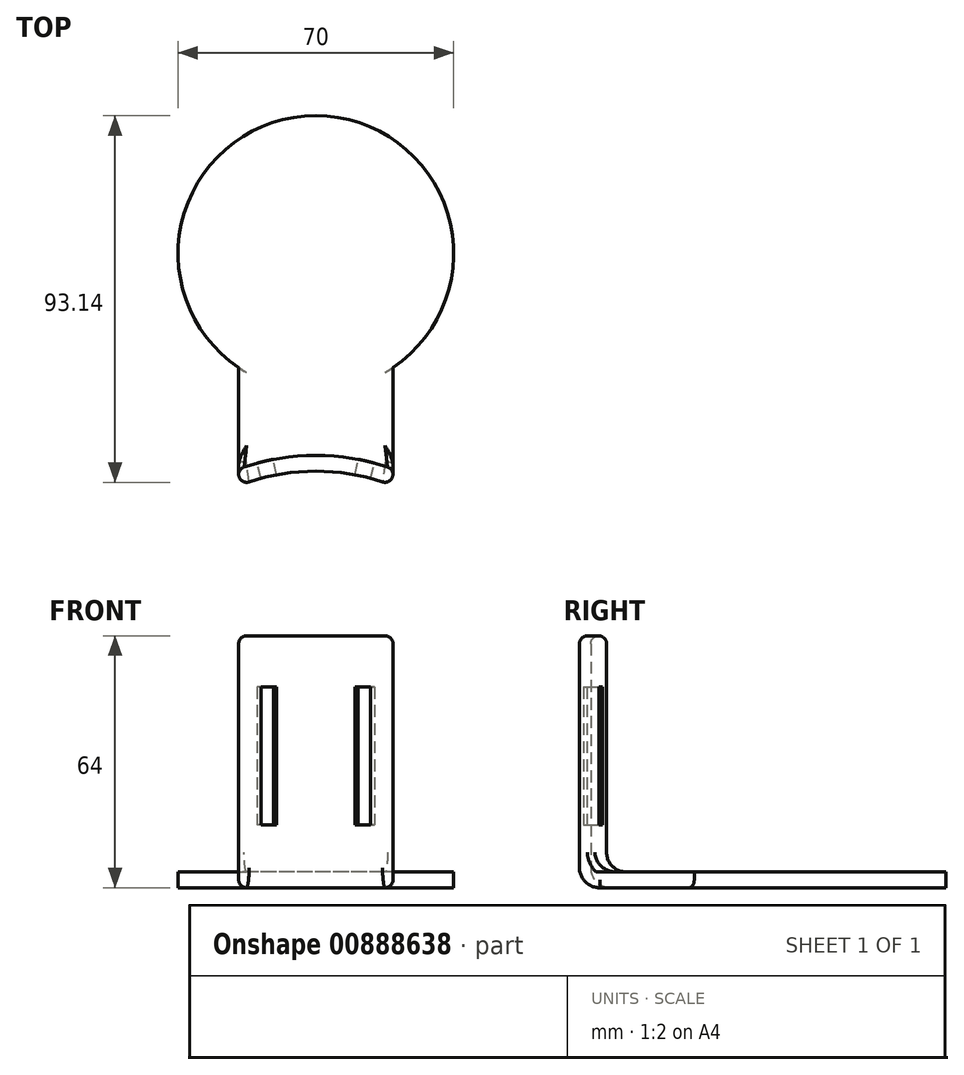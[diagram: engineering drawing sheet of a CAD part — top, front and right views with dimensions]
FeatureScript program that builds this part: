
annotation { "Feature Type Name" : "Feature", "Feature Type Description" : "" }
export const myFeature = defineFeature(function(context is Context, id is Id, definition is map)
    precondition{}
    {
        {
            var Q0;
            Q0=qCreatedBy(makeId("Top.planeOp"),FACE);
            var sketch = newSketch(context, id + "F0", { "sketchPlane" : qUnion([Q0])});
            skCircle(sketch, "E0", {"center": v(0, 0) * mm, "radius": 35 * mm});
            skLineSegment(sketch, "E1", {"start": v(0, 0) * mm, "end": v(0, -81.88) * mm, "construction": true});
            skLineSegment(sketch, "E2", {"start": v(19.6, -29) * mm, "end": v(19.6, -59) * mm});
            skLineSegment(sketch, "E3.MirrorCS", {"start": v(-19.6, -29) * mm, "end": v(-19.6, -59) * mm});
            skLineSegment(sketch, "E4", {"start": v(-35.4, 35) * mm, "end": v(46.06, 35) * mm, "construction": true});
            skArc(sketch, "E5", {"start": v(19.6, -59) * mm, "mid": v(0, -55.28) * mm, "end": v(-19.6, -59) * mm});
            skPoint(sketch, "E6", {"position": v(10, -56.22) * mm});
            skPoint(sketch, "E7", {"position": v(13.9, -57.12) * mm});
            skPoint(sketch, "E8.MirrorP", {"position": v(-10, -56.22) * mm});
            skPoint(sketch, "E9.MirrorP", {"position": v(-13.9, -57.12) * mm});
            skArc(sketch, "E10.0", {"start": v(19.6, -54.72) * mm, "mid": v(0, -51.28) * mm, "end": v(-19.6, -54.72) * mm});
            skSolve(sketch);
        }
        {
            var Q0;
            {var subQ0=sQuery(id+"F0.wireOp",EDGE,"E0");var subQ1=makeQuery(id+"F0.imprint","INTERSECT",VERTEX,{"derivedFrom":[subQ0,sQuery(id+"F0.wireOp",EDGE,"E2")]});Q0=makeQuery(id+"F0.imprint","IMPRINT",FACE,{"disambiguationData":[TD([[makeQuery(id+"F0.imprint","IMPRINT",EDGE,{"disambiguationData":[TD([[subQ1,1.0]])],"derivedFrom":subQ0}),1.0]])]});}
            var Q1;
            {var subQ5=sQuery(id+"F0.wireOp",EDGE,"E10.0");Q1=makeQuery(id+"F0.imprint","IMPRINT",FACE,{"disambiguationData":[TD([[makeQuery(id+"F0.imprint","IMPRINT",EDGE,{"derivedFrom":subQ5}),-1.0]])]});}
            var Q2;
            {var subQ0=sQuery(id+"F0.wireOp",EDGE,"E5");Q2=makeQuery(id+"F0.imprint","IMPRINT",FACE,{"disambiguationData":[TD([[makeQuery(id+"F0.imprint","IMPRINT",EDGE,{"derivedFrom":subQ0}),-1.0]])]});}
            extrude(context, id + "F1", {"entities" : qUnion([Q0, Q1, Q2]), "depth" : 4 * mm, "offsetDistance" : 25 * mm});
        }
        {
            var Q0;
            {var subQ0=sQuery(id+"F0.wireOp",EDGE,"E5");Q0=makeQuery(id+"F0.imprint","IMPRINT",FACE,{"disambiguationData":[TD([[makeQuery(id+"F0.imprint","IMPRINT",EDGE,{"derivedFrom":subQ0}),-1.0]])]});}
            extrude(context, id + "F2", {"entities" : qUnion([Q0]), "operationType" : NewBodyOperationType.ADD, "depth" : 64 * mm, "offsetDistance" : 25 * mm});
        }
        {
            var Q0;
            Q0=qCreatedBy(makeId("Top.planeOp"),FACE);
            cPlane(context, id + "F3", {"entities" : qUnion([Q0]), "cplaneType" : CPlaneType.OFFSET, "offset" : 16 * mm, "width" : 150 * mm, "height" : 150 * mm});
        }
        {
            var Q0;
            Q0=qCreatedBy(id+"F3.planeOp",FACE);
            var sketch = newSketch(context, id + "F4", { "sketchPlane" : qUnion([Q0])});
            skPoint(sketch, "E11.0", {"position": v(13.9, -57.12) * mm});
            skPoint(sketch, "E11.1", {"position": v(10, -56.22) * mm});
            skPoint(sketch, "E11.2", {"position": v(-10, -56.22) * mm});
            skPoint(sketch, "E11.3", {"position": v(-13.9, -57.12) * mm});
            skArc(sketch, "E11.4", {"start": v(19.6, -59) * mm, "mid": v(0, -55.28) * mm, "end": v(-19.6, -59) * mm});
            skArc(sketch, "E11.5", {"start": v(19.6, -54.72) * mm, "mid": v(0, -51.28) * mm, "end": v(-19.6, -54.72) * mm});
            skLineSegment(sketch, "E12", {"start": v(13.9, -57.12) * mm, "end": v(14.94, -53.26) * mm});
            skLineSegment(sketch, "E13", {"start": v(10, -56.22) * mm, "end": v(10.75, -52.3) * mm});
            skLineSegment(sketch, "E14.MirrorCS", {"start": v(-13.9, -57.12) * mm, "end": v(-14.94, -53.26) * mm});
            skLineSegment(sketch, "E15.MirrorCS", {"start": v(-10, -56.22) * mm, "end": v(-10.75, -52.3) * mm});
            skSolve(sketch);
        }
        {
            var Q0;
            {var subQ0=sQuery(id+"F4.wireOp",EDGE,"E12");Q0=makeQuery(id+"F4.imprint","IMPRINT",FACE,{"disambiguationData":[TD([[makeQuery(id+"F4.imprint","IMPRINT",EDGE,{"derivedFrom":subQ0}),1.0]])]});}
            var Q1;
            {var subQ0=sQuery(id+"F4.wireOp",EDGE,"E14.MirrorCS");Q1=makeQuery(id+"F4.imprint","IMPRINT",FACE,{"disambiguationData":[TD([[makeQuery(id+"F4.imprint","IMPRINT",EDGE,{"derivedFrom":subQ0}),-1.0]])]});}
            extrude(context, id + "F5", {"entities" : qUnion([Q0, Q1]), "operationType" : NewBodyOperationType.REMOVE, "depth" : 35 * mm, "offsetDistance" : 25 * mm});
        }
        {
            var Q0;
            Q0=makeQuery(id+"F1.opExtrude","CAP_EDGE",EDGE,{"disambiguationData":[OSD([sQuery(id+"F0.wireOp",EDGE,"E5")])],"isStart":true});
            var Q1;
            Q1=makeQuery(id+"F2.boolean.opBoolean","INTERSECT",EDGE,{"derivedFrom":[makeQuery(id+"F1.opExtrude","CAP_FACE",FACE,{"disambiguationData":[OSD([sQuery(id+"F0.wireOp",EDGE,"E0"),sQuery(id+"F0.wireOp",EDGE,"E2"),sQuery(id+"F0.wireOp",EDGE,"E3.MirrorCS"),sQuery(id+"F0.wireOp",EDGE,"E5")])],"isStart":false}),makeQuery(id+"F2.opExtrude","SWEPT_FACE",FACE,{"disambiguationData":[OSD([sQuery(id+"F0.wireOp",EDGE,"E10.0")])]})]});
            fillet(context, id + "F6", {"entities" : qUnion([Q0, Q1]), "radius" : 5 * mm, "tangentPropagation" : true, "allowEdgeOverflow" : false});
        }
        {
            var Q0;
            Q0=makeQuery(id+"F2.opExtrude","SWEPT_EDGE",EDGE,{"disambiguationData":[OSD([sQuery(id+"F0.wireOp",EDGE,"E3.MirrorCS"),sQuery(id+"F0.wireOp",EDGE,"E10.0")])]});
            var Q1;
            {var subQ0=sQuery(id+"F0.wireOp",EDGE,"E5");var subQ1=sQuery(id+"F0.wireOp",EDGE,"E3.MirrorCS");Q1=makeQuery(id+"F2.boolean.opBoolean","MERGE",EDGE,{"derivedFrom":[makeQuery(id+"F1.opExtrude","SWEPT_EDGE",EDGE,{"disambiguationData":[OSD([subQ1,subQ0])]}),makeQuery(id+"F2.opExtrude","SWEPT_EDGE",EDGE,{"disambiguationData":[OSD([subQ1,subQ0])]})]});}
            var Q2;
            {var subQ0=sQuery(id+"F0.wireOp",EDGE,"E5");var subQ1=sQuery(id+"F0.wireOp",EDGE,"E2");Q2=makeQuery(id+"F2.boolean.opBoolean","MERGE",EDGE,{"derivedFrom":[makeQuery(id+"F1.opExtrude","SWEPT_EDGE",EDGE,{"disambiguationData":[OSD([subQ1,subQ0])]}),makeQuery(id+"F2.opExtrude","SWEPT_EDGE",EDGE,{"disambiguationData":[OSD([subQ1,subQ0])]})]});}
            var Q3;
            Q3=makeQuery(id+"F2.opExtrude","SWEPT_EDGE",EDGE,{"disambiguationData":[OSD([sQuery(id+"F0.wireOp",EDGE,"E2"),sQuery(id+"F0.wireOp",EDGE,"E10.0")])]});
            fillet(context, id + "F7", {"entities" : qUnion([Q0, Q1, Q2, Q3]), "radius" : 2 * mm, "tangentPropagation" : true, "allowEdgeOverflow" : false});
        }
        {
            var Q0;
            Q0=makeQuery(id+"F2.opExtrude","CAP_EDGE",EDGE,{"disambiguationData":[OSD([sQuery(id+"F0.wireOp",EDGE,"E10.0")])],"isStart":false});
            var Q1;
            Q1=makeQuery(id+"F2.opExtrude","CAP_EDGE",EDGE,{"disambiguationData":[OSD([sQuery(id+"F0.wireOp",EDGE,"E5")])],"isStart":false});
            var Q2;
            Q2=makeQuery(id+"F5.boolean.opBoolean","COPY",EDGE,{"derivedFrom":makeQuery(id+"F5.opExtrude","SWEPT_EDGE",EDGE,{"disambiguationData":[OSD([sQuery(id+"F4.wireOp",EDGE,"E11.5"),sQuery(id+"F4.wireOp",EDGE,"E15.MirrorCS")])]})});
            var Q3;
            Q3=makeQuery(id+"F5.boolean.opBoolean","COPY",EDGE,{"derivedFrom":makeQuery(id+"F5.opExtrude","SWEPT_EDGE",EDGE,{"disambiguationData":[OSD([sQuery(id+"F4.wireOp",EDGE,"E11.5"),sQuery(id+"F4.wireOp",EDGE,"E13")])]})});
            var Q4;
            Q4=makeQuery(id+"F5.boolean.opBoolean","COPY",EDGE,{"derivedFrom":makeQuery(id+"F5.opExtrude","SWEPT_EDGE",EDGE,{"disambiguationData":[OSD([sQuery(id+"F4.wireOp",EDGE,"E11.4"),sQuery(id+"F4.wireOp",EDGE,"E14.MirrorCS")])]})});
            var Q5;
            Q5=makeQuery(id+"F5.boolean.opBoolean","COPY",EDGE,{"derivedFrom":makeQuery(id+"F5.opExtrude","SWEPT_EDGE",EDGE,{"disambiguationData":[OSD([sQuery(id+"F4.wireOp",EDGE,"E11.4"),sQuery(id+"F4.wireOp",EDGE,"E12")])]})});
            fillet(context, id + "F8", {"entities" : qUnion([Q0, Q1, Q2, Q3, Q4, Q5]), "radius" : 2 * mm, "tangentPropagation" : true, "allowEdgeOverflow" : false});
        }
    });
